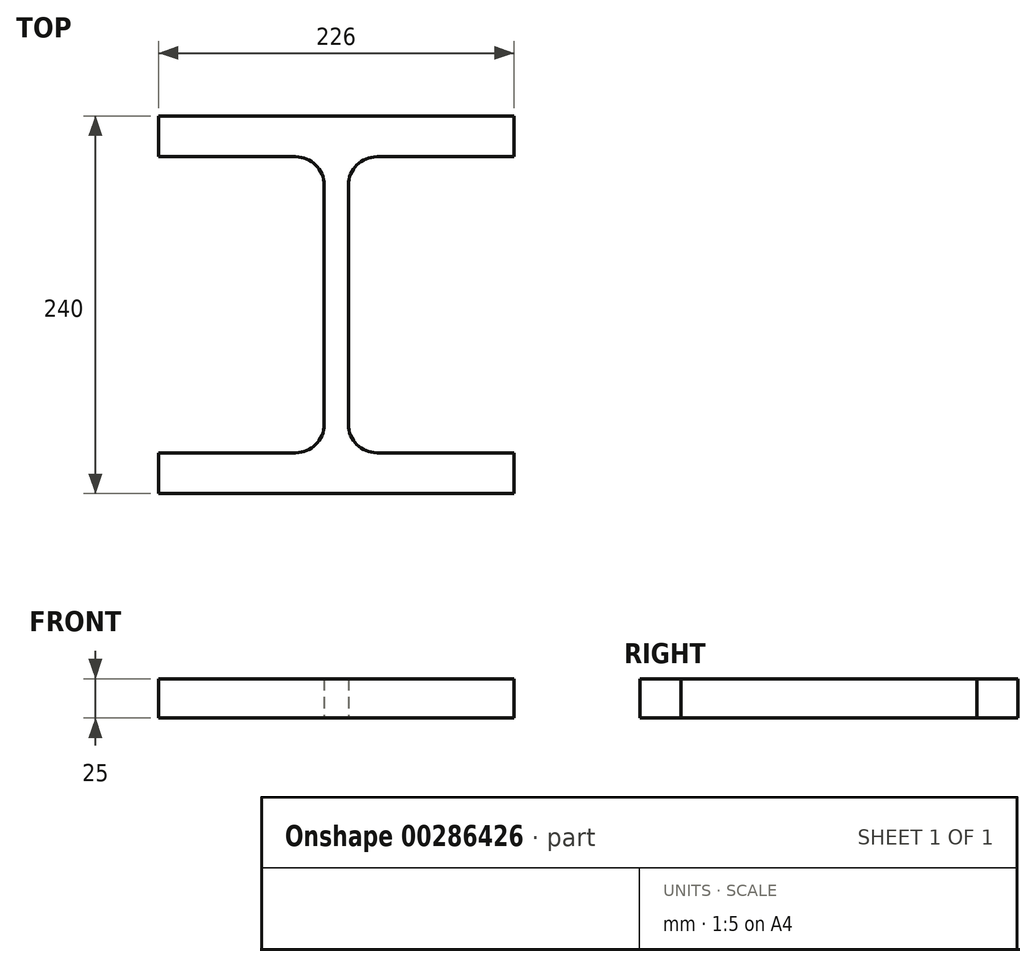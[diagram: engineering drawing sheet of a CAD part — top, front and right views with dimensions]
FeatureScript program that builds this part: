
annotation { "Feature Type Name" : "Feature", "Feature Type Description" : "" }
export const myFeature = defineFeature(function(context is Context, id is Id, definition is map)
    precondition{}
    {
        {
            var Q0;
            Q0=qCreatedBy(makeId("Top.planeOp"),FACE);
            var sketch = newSketch(context, id + "F0", { "sketchPlane" : qUnion([Q0])});
            skLineSegment(sketch, "E0", {"start": v(-121.55, 143.06) * mm, "end": v(-121.55, 169.06) * mm});
            skLineSegment(sketch, "E1", {"start": v(-121.55, 169.06) * mm, "end": v(104.45, 169.06) * mm});
            skLineSegment(sketch, "E2", {"start": v(104.45, 169.06) * mm, "end": v(104.45, 143.06) * mm});
            skLineSegment(sketch, "E3", {"start": v(104.45, 143.06) * mm, "end": v(17.2, 143.06) * mm});
            skLineSegment(sketch, "E4", {"start": v(-0.8, 125.06) * mm, "end": v(-0.8, -26.94) * mm});
            skLineSegment(sketch, "E5", {"start": v(17.2, -44.94) * mm, "end": v(104.45, -44.94) * mm});
            skLineSegment(sketch, "E6", {"start": v(104.45, -44.94) * mm, "end": v(104.45, -70.94) * mm});
            skLineSegment(sketch, "E7", {"start": v(104.45, -70.94) * mm, "end": v(-121.55, -70.94) * mm});
            skLineSegment(sketch, "E8", {"start": v(-121.55, -70.94) * mm, "end": v(-121.55, -44.94) * mm});
            skLineSegment(sketch, "E9", {"start": v(-121.55, -44.94) * mm, "end": v(-34.3, -44.94) * mm});
            skLineSegment(sketch, "E10", {"start": v(-16.3, -26.94) * mm, "end": v(-16.3, 125.06) * mm});
            skLineSegment(sketch, "E11", {"start": v(-34.3, 143.06) * mm, "end": v(-121.55, 143.06) * mm});
            skPoint(sketch, "E12.visualSharp", {"position": v(-16.3, 143.06) * mm});
            skArc(sketch, "E12.filletArc", {"start": v(-16.3, 125.06) * mm, "mid": v(-21.57, 137.79) * mm, "end": v(-34.3, 143.06) * mm});
            skPoint(sketch, "E13.visualSharp", {"position": v(-0.8, 143.06) * mm});
            skArc(sketch, "E13.filletArc", {"start": v(17.2, 143.06) * mm, "mid": v(4.48, 137.79) * mm, "end": v(-0.8, 125.06) * mm});
            skPoint(sketch, "E14.visualSharp", {"position": v(-16.3, -44.94) * mm});
            skArc(sketch, "E14.filletArc", {"start": v(-34.3, -44.94) * mm, "mid": v(-21.57, -39.67) * mm, "end": v(-16.3, -26.94) * mm});
            skPoint(sketch, "E15.visualSharp", {"position": v(-0.8, -44.94) * mm});
            skArc(sketch, "E15.filletArc", {"start": v(-0.8, -26.94) * mm, "mid": v(4.48, -39.67) * mm, "end": v(17.2, -44.94) * mm});
            skSolve(sketch);
        }
        {
            var Q0;
            Q0 = qSketchRegion(id + "F0", true);
            extrude(context, id + "F1", {"entities" : qUnion([Q0]), "depth" : 25 * mm});
        }
    });
